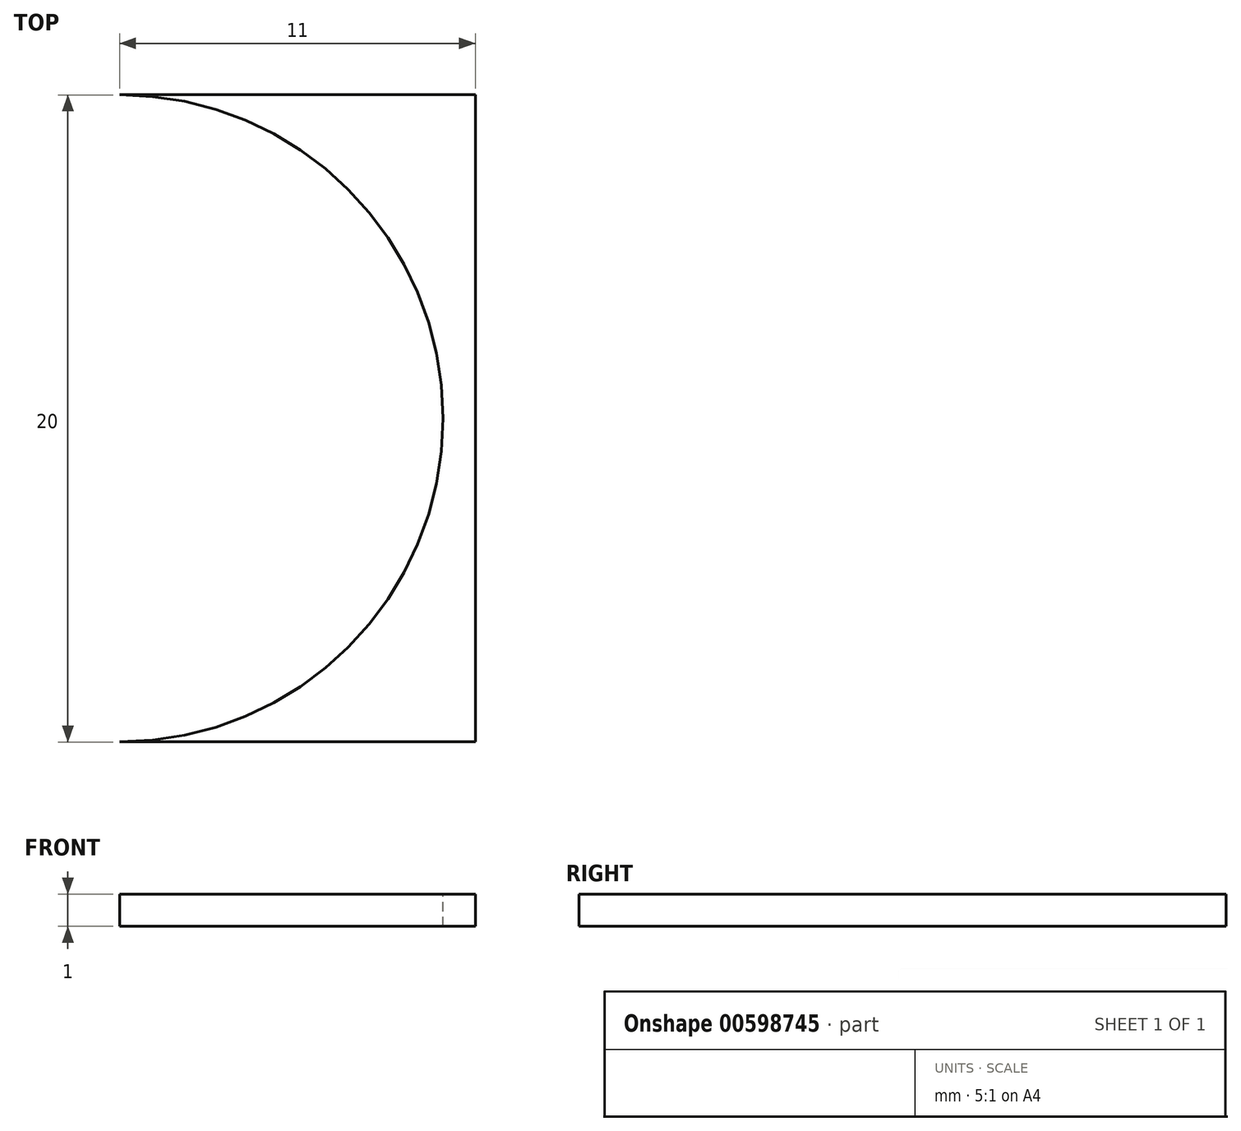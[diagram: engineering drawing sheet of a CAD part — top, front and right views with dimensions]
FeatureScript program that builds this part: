
annotation { "Feature Type Name" : "Feature", "Feature Type Description" : "" }
export const myFeature = defineFeature(function(context is Context, id is Id, definition is map)
    precondition{}
    {
        {
            var Q0;
            Q0=qCreatedBy(makeId("Top.planeOp"),FACE);
            var sketch = newSketch(context, id + "F0", { "sketchPlane" : qUnion([Q0])});
            skLineSegment(sketch, "E0.bottom", {"start": v(-5.5, 13.03) * mm, "end": v(5.5, 13.03) * mm});
            skLineSegment(sketch, "E0.top", {"start": v(-5.5, -6.97) * mm, "end": v(5.5, -6.97) * mm});
            skLineSegment(sketch, "E0.left", {"start": v(-5.5, 13.03) * mm, "end": v(-5.5, -6.97) * mm});
            skLineSegment(sketch, "E0.right", {"start": v(5.5, 13.03) * mm, "end": v(5.5, -6.97) * mm});
            skPoint(sketch, "E0.middle", {"position": v(0, 3.03) * mm});
            skSolve(sketch);
        }
        {
            var Q0;
            Q0=makeQuery(id+"F0.imprint","IMPRINT",FACE,{"disambiguationData":[TD([[makeQuery(id+"F0.imprint","IMPRINT",EDGE,{"derivedFrom":sQuery(id+"F0.wireOp",EDGE,"E0.bottom")}),-1.0]])]});
            extrude(context, id + "F1", {"entities" : qUnion([Q0]), "depth" : 1 * mm, "offsetDistance" : 25.4 * mm});
        }
        {
            var Q0;
            Q0=makeQuery(id+"F1.opExtrude","CAP_FACE",FACE,{"disambiguationData":[OSD([sQuery(id+"F0.wireOp",EDGE,"E0.bottom"),sQuery(id+"F0.wireOp",EDGE,"E0.top"),sQuery(id+"F0.wireOp",EDGE,"E0.left"),sQuery(id+"F0.wireOp",EDGE,"E0.right")])],"isStart":false});
            var sketch = newSketch(context, id + "F2", { "sketchPlane" : qUnion([Q0])});
            skLineSegment(sketch, "E1", {"start": v(5.5, 3.03) * mm, "end": v(4.5, 3.03) * mm});
            skCircle(sketch, "E2", {"center": v(-5.5, 3.03) * mm, "radius": 10 * mm});
            skPoint(sketch, "E2.first.point", {"position": v(-5.5, -6.97) * mm});
            skPoint(sketch, "E2.second.point", {"position": v(-5.5, 13.03) * mm});
            skSolve(sketch);
        }
        {
            var Q0;
            {var subQ1=makeQuery(id+"F1.opExtrude","CAP_EDGE",EDGE,{"disambiguationData":[OSD([sQuery(id+"F0.wireOp",EDGE,"E0.left")])],"isStart":false});Q0=makeQuery(id+"F2.imprint","IMPRINT",FACE,{"disambiguationData":[TD([[makeQuery(id+"F2.imprint","IMPRINT",EDGE,{"derivedFrom":subQ1}),1.0]])]});}
            extrude(context, id + "F3", {"entities" : qUnion([Q0]), "operationType" : NewBodyOperationType.REMOVE, "oppositeDirection" : true, "depth" : 25.4 * mm, "offsetDistance" : 25.4 * mm, "hasSecondDirection" : true, "secondDirectionOppositeDirection" : false, "secondDirectionDepth" : 25.4 * mm});
        }
    });
